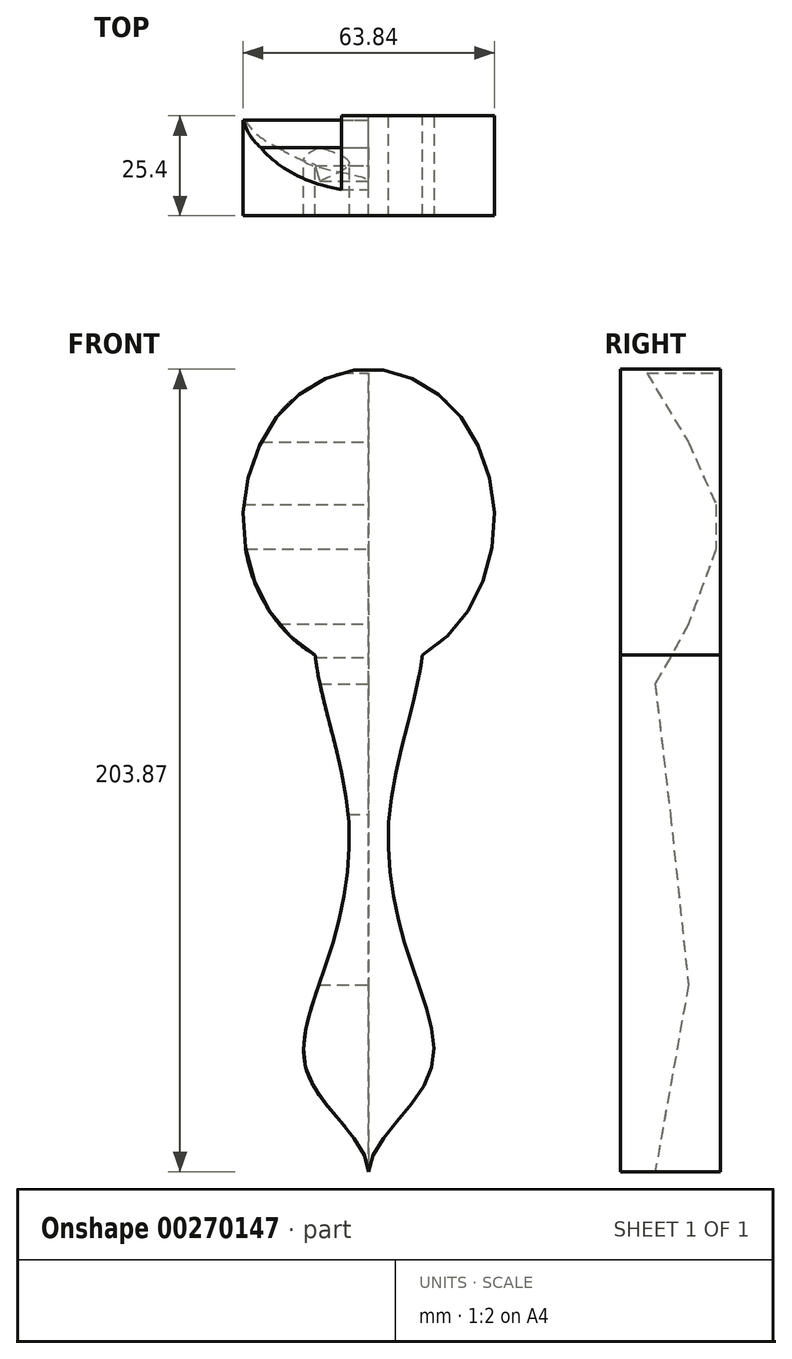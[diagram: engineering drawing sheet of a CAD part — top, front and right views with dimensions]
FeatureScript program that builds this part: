
annotation { "Feature Type Name" : "Feature", "Feature Type Description" : "" }
export const myFeature = defineFeature(function(context is Context, id is Id, definition is map)
    precondition{}
    {
        {
            var Q0;
            Q0=qCreatedBy(makeId("Front.planeOp"),FACE);
            var sketch = newSketch(context, id + "F0", { "sketchPlane" : qUnion([Q0])});
            skEllipse(sketch, "E0", {"center": v(0, 74.97) * mm, "majorRadius": 38.1 * mm, "minorRadius": 31.92 * mm, "majorAxis": v(0, -1)});
            skFitSpline(sketch, "E1", {"points": [v(-13.63, 40.52) * mm, v(-5.2, 0) * mm, v(-11.13, -38.98) * mm, v(-15.12, -66.9) * mm, v(0, -90.8) * mm], "startDerivative": vector(14.76, -135.17) * mm, "endDerivative": vector(0, -99.7) * mm});
            skLineSegment(sketch, "E2", {"start": v(0, 123.95) * mm, "end": v(0, -97.5) * mm, "construction": true});
            skPoint(sketch, "E2.startSnap0", {"position": v(0, 113.07) * mm});
            skFitSpline(sketch, "E3.MirrorCS", {"points": [v(13.63, 40.52) * mm, v(5.2, 0) * mm, v(11.13, -38.98) * mm, v(15.12, -66.9) * mm, v(0, -90.8) * mm], "startDerivative": vector(-14.76, -135.17) * mm, "endDerivative": vector(0, -99.7) * mm});
            skLineSegment(sketch, "E4", {"start": v(-12.82, 35.22) * mm, "end": v(0, 26.06) * mm});
            skPoint(sketch, "E5.orphan", {"position": v(-96.53, 40.52) * mm});
            skPoint(sketch, "E6.orphan", {"position": v(-92.6, -5.7) * mm});
            skPoint(sketch, "E7.orphan", {"position": v(116.88, 66.15) * mm});
            skLineSegment(sketch, "E8", {"start": v(12.82, 35.22) * mm, "end": v(0, 26.06) * mm});
            skSolve(sketch);
        }
        {
            var Q0;
            Q0 = qSketchRegion(id + "F0", true);
            extrude(context, id + "F1", {"entities" : qUnion([Q0]), "endBound" : BoundingType.SYMMETRIC, "depth" : 25.4 * mm});
        }
        {
            var Q0;
            Q0=qCreatedBy(makeId("Right.planeOp"),FACE);
            var sketch = newSketch(context, id + "F2", { "sketchPlane" : qUnion([Q0])});
            skLineSegment(sketch, "E9", {"start": v(-6, 112.17) * mm, "end": v(4.58, 94.54) * mm});
            skLineSegment(sketch, "E10", {"start": v(4.58, 94.54) * mm, "end": v(11.64, 78.67) * mm});
            skLineSegment(sketch, "E11", {"start": v(11.64, 78.67) * mm, "end": v(11.64, 67.38) * mm});
            skLineSegment(sketch, "E12", {"start": v(11.64, 67.38) * mm, "end": v(4.58, 48.34) * mm});
            skLineSegment(sketch, "E13", {"start": v(4.58, 48.34) * mm, "end": v(0, 39.87) * mm});
            skLineSegment(sketch, "E14", {"start": v(0, 39.87) * mm, "end": v(-3.88, 33.17) * mm});
            skLineSegment(sketch, "E15", {"start": v(-3.88, 33.17) * mm, "end": v(0, 0) * mm});
            skLineSegment(sketch, "E16", {"start": v(0, 0) * mm, "end": v(4.58, -43.35) * mm});
            skLineSegment(sketch, "E17", {"start": v(4.58, -43.35) * mm, "end": v(-3.88, -90.96) * mm});
            skLineSegment(sketch, "E18", {"start": v(-6, 112.17) * mm, "end": v(53.25, 112.17) * mm});
            skLineSegment(sketch, "E19", {"start": v(53.25, 112.17) * mm, "end": v(43.02, -94.84) * mm});
            skLineSegment(sketch, "E20", {"start": v(43.02, -94.84) * mm, "end": v(-3.88, -90.96) * mm});
            skSolve(sketch);
        }
        {
            var Q0;
            Q0=makeQuery(id+"F2.imprint","IMPRINT",FACE,{"disambiguationData":[TD([[makeQuery(id+"F2.imprint","IMPRINT",EDGE,{"derivedFrom":sQuery(id+"F2.wireOp",EDGE,"E9")}),1.0]])]});
            extrude(context, id + "F3", {"entities" : qUnion([Q0]), "operationType" : NewBodyOperationType.REMOVE, "oppositeDirection" : true, "depth" : 406.4 * mm});
        }
    });
